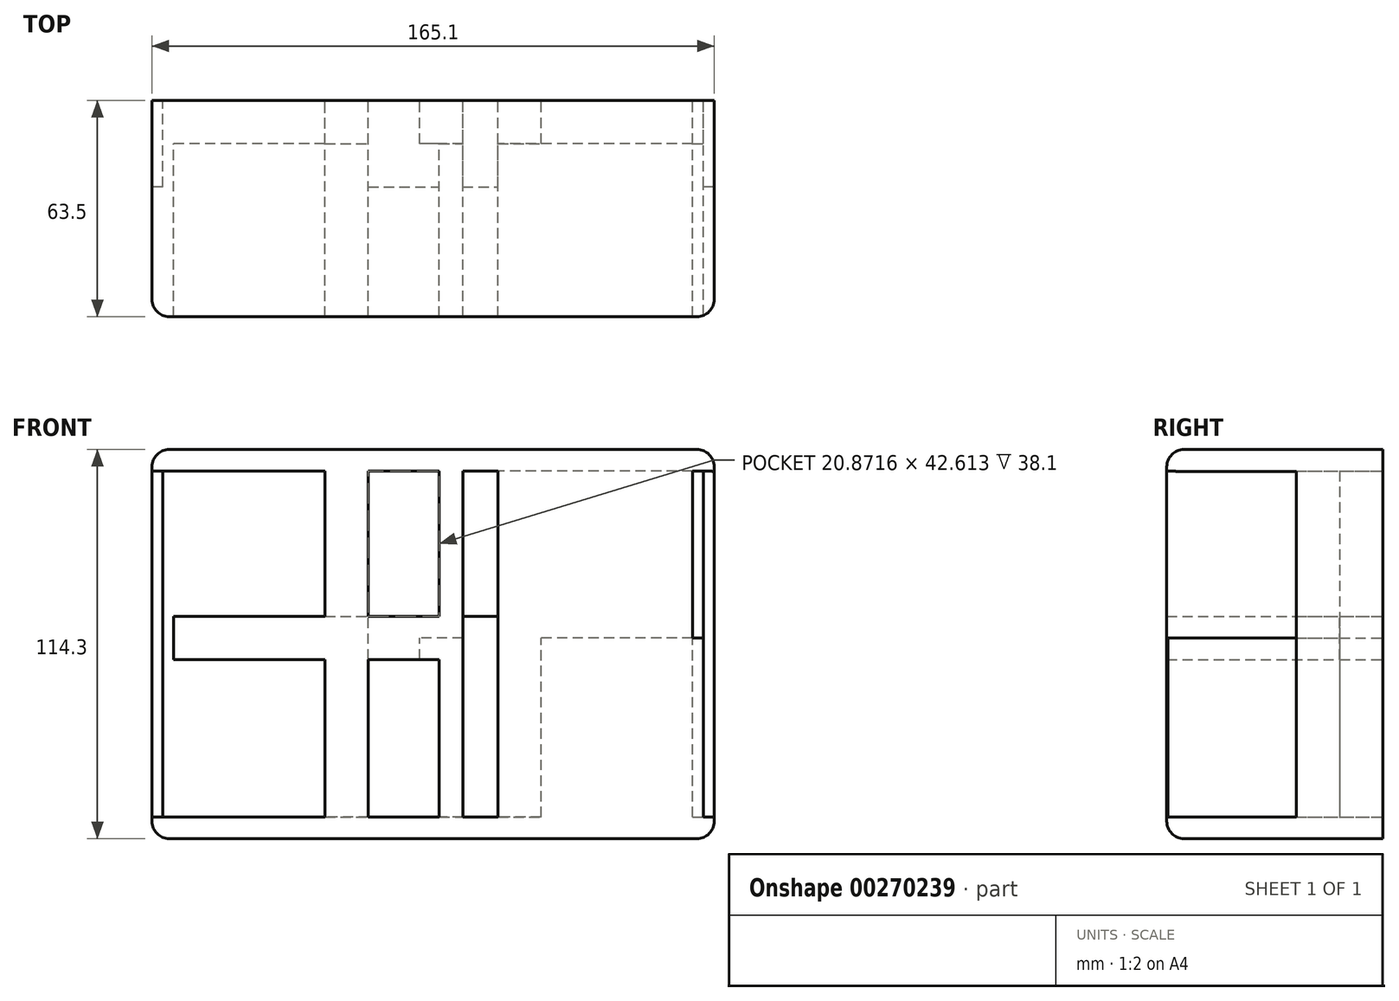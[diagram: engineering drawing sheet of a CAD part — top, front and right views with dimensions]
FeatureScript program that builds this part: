
annotation { "Feature Type Name" : "Feature", "Feature Type Description" : "" }
export const myFeature = defineFeature(function(context is Context, id is Id, definition is map)
    precondition{}
    {
        {
            var Q0;
            Q0=qCreatedBy(makeId("Front.planeOp"),FACE);
            var sketch = newSketch(context, id + "F0", { "sketchPlane" : qUnion([Q0])});
            skLineSegment(sketch, "E0", {"start": v(0, 0) * mm, "end": v(0, 48.96) * mm});
            skLineSegment(sketch, "E1", {"start": v(0, 48.96) * mm, "end": v(0, -52.64) * mm});
            skLineSegment(sketch, "E2", {"start": v(0, 0) * mm, "end": v(-78.02, 0) * mm});
            skLineSegment(sketch, "E3", {"start": v(-78.02, 0) * mm, "end": v(74.38, 0) * mm});
            skLineSegment(sketch, "E4.bottom", {"start": v(-78.02, 0) * mm, "end": v(0, 0) * mm});
            skLineSegment(sketch, "E4.top", {"start": v(-78.02, 48.96) * mm, "end": v(0, 48.96) * mm});
            skLineSegment(sketch, "E4.left", {"start": v(-78.02, 0) * mm, "end": v(-78.02, 48.96) * mm});
            skLineSegment(sketch, "E5.bottom", {"start": v(0, 48.96) * mm, "end": v(74.38, 48.96) * mm});
            skLineSegment(sketch, "E5.top", {"start": v(0, 0) * mm, "end": v(74.38, 0) * mm});
            skLineSegment(sketch, "E5.right", {"start": v(74.38, 48.96) * mm, "end": v(74.38, 0) * mm});
            skLineSegment(sketch, "E6.bottom", {"start": v(74.38, 0) * mm, "end": v(0, 0) * mm});
            skLineSegment(sketch, "E6.top", {"start": v(74.38, -52.64) * mm, "end": v(0, -52.64) * mm});
            skLineSegment(sketch, "E6.left", {"start": v(74.38, 0) * mm, "end": v(74.38, -52.64) * mm});
            skLineSegment(sketch, "E6.right", {"start": v(0, 0) * mm, "end": v(0, -52.64) * mm});
            skLineSegment(sketch, "E7.bottom", {"start": v(0, -52.64) * mm, "end": v(-78.02, -52.64) * mm});
            skLineSegment(sketch, "E7.right", {"start": v(-78.02, -52.64) * mm, "end": v(-78.02, 0) * mm});
            skLineSegment(sketch, "E8", {"start": v(0, 48.96) * mm, "end": v(0, 55.31) * mm});
            skLineSegment(sketch, "E9", {"start": v(-78.02, 0) * mm, "end": v(-84.37, 0) * mm});
            skLineSegment(sketch, "E10", {"start": v(0, -52.64) * mm, "end": v(0, -58.99) * mm});
            skLineSegment(sketch, "E11", {"start": v(74.38, 0) * mm, "end": v(80.73, 0) * mm});
            skLineSegment(sketch, "E12.top", {"start": v(-78.02, 55.31) * mm, "end": v(0, 55.31) * mm});
            skLineSegment(sketch, "E12.left", {"start": v(-78.02, 48.96) * mm, "end": v(-78.02, 55.31) * mm});
            skLineSegment(sketch, "E13.bottom", {"start": v(74.38, 48.96) * mm, "end": v(0, 48.96) * mm});
            skLineSegment(sketch, "E13.top", {"start": v(74.38, 55.31) * mm, "end": v(0, 55.31) * mm});
            skLineSegment(sketch, "E13.left", {"start": v(74.38, 48.96) * mm, "end": v(74.38, 55.31) * mm});
            skLineSegment(sketch, "E14.bottom", {"start": v(80.73, 0) * mm, "end": v(74.38, 0) * mm});
            skLineSegment(sketch, "E14.top", {"start": v(80.73, 55.31) * mm, "end": v(74.38, 55.31) * mm});
            skLineSegment(sketch, "E14.left", {"start": v(80.73, 0) * mm, "end": v(80.73, 55.31) * mm});
            skLineSegment(sketch, "E14.right", {"start": v(74.38, 0) * mm, "end": v(74.38, 55.31) * mm});
            skLineSegment(sketch, "E15.top", {"start": v(80.73, -52.64) * mm, "end": v(74.38, -52.64) * mm});
            skLineSegment(sketch, "E15.left", {"start": v(80.73, 0) * mm, "end": v(80.73, -52.64) * mm});
            skLineSegment(sketch, "E16.bottom", {"start": v(0, -58.99) * mm, "end": v(80.73, -58.99) * mm});
            skLineSegment(sketch, "E16.top", {"start": v(0, -52.64) * mm, "end": v(80.73, -52.64) * mm});
            skLineSegment(sketch, "E16.left", {"start": v(0, -58.99) * mm, "end": v(0, -52.64) * mm});
            skLineSegment(sketch, "E16.right", {"start": v(80.73, -58.99) * mm, "end": v(80.73, -52.64) * mm});
            skLineSegment(sketch, "E17.bottom", {"start": v(-78.02, -52.64) * mm, "end": v(0, -52.64) * mm});
            skLineSegment(sketch, "E17.top", {"start": v(-78.02, -58.99) * mm, "end": v(0, -58.99) * mm});
            skLineSegment(sketch, "E17.left", {"start": v(-78.02, -52.64) * mm, "end": v(-78.02, -58.99) * mm});
            skLineSegment(sketch, "E18.bottom", {"start": v(-84.37, 0) * mm, "end": v(-78.02, 0) * mm});
            skLineSegment(sketch, "E18.top", {"start": v(-84.37, -58.99) * mm, "end": v(-78.02, -58.99) * mm});
            skLineSegment(sketch, "E18.left", {"start": v(-84.37, 0) * mm, "end": v(-84.37, -58.99) * mm});
            skLineSegment(sketch, "E18.right", {"start": v(-78.02, 0) * mm, "end": v(-78.02, -58.99) * mm});
            skLineSegment(sketch, "E19.bottom", {"start": v(-78.02, 55.31) * mm, "end": v(-84.37, 55.31) * mm});
            skLineSegment(sketch, "E19.left", {"start": v(-78.02, 55.31) * mm, "end": v(-78.02, 0) * mm});
            skLineSegment(sketch, "E19.right", {"start": v(-84.37, 55.31) * mm, "end": v(-84.37, 0) * mm});
            skLineSegment(sketch, "E20", {"start": v(-78.02, -52.64) * mm, "end": v(-27.22, -52.64) * mm});
            skLineSegment(sketch, "E21", {"start": v(-27.22, -52.64) * mm, "end": v(74.38, -52.64) * mm});
            skLineSegment(sketch, "E22", {"start": v(74.38, -52.64) * mm, "end": v(23.58, -52.64) * mm});
            skLineSegment(sketch, "E23", {"start": v(-27.22, -52.64) * mm, "end": v(-27.22, 48.96) * mm});
            skLineSegment(sketch, "E24", {"start": v(23.58, -52.64) * mm, "end": v(23.58, 48.96) * mm});
            skLineSegment(sketch, "E25", {"start": v(0, 48.96) * mm, "end": v(-5.81, 48.96) * mm});
            skLineSegment(sketch, "E26", {"start": v(-5.81, 48.96) * mm, "end": v(6.89, 48.96) * mm});
            skLineSegment(sketch, "E27", {"start": v(-5.81, 48.96) * mm, "end": v(-5.81, -52.64) * mm});
            skLineSegment(sketch, "E28", {"start": v(6.89, 48.96) * mm, "end": v(6.89, -52.64) * mm});
            skLineSegment(sketch, "E29", {"start": v(-27.22, 48.96) * mm, "end": v(-33.57, 48.96) * mm});
            skLineSegment(sketch, "E30", {"start": v(-33.57, 48.96) * mm, "end": v(-20.87, 48.96) * mm});
            skLineSegment(sketch, "E31", {"start": v(23.58, 48.96) * mm, "end": v(17.23, 48.96) * mm});
            skLineSegment(sketch, "E32", {"start": v(17.23, 48.96) * mm, "end": v(29.93, 48.96) * mm});
            skLineSegment(sketch, "E33", {"start": v(-33.57, 48.96) * mm, "end": v(-33.57, -52.64) * mm});
            skLineSegment(sketch, "E34", {"start": v(-20.87, 48.96) * mm, "end": v(-20.87, -52.64) * mm});
            skLineSegment(sketch, "E35", {"start": v(17.23, 48.96) * mm, "end": v(17.23, -52.64) * mm});
            skLineSegment(sketch, "E36", {"start": v(29.93, 48.96) * mm, "end": v(29.93, -52.64) * mm});
            skLineSegment(sketch, "E37", {"start": v(74.38, 0) * mm, "end": v(74.38, 6.35) * mm});
            skLineSegment(sketch, "E38", {"start": v(74.38, 6.35) * mm, "end": v(74.38, -6.35) * mm});
            skLineSegment(sketch, "E39", {"start": v(74.38, -6.35) * mm, "end": v(-78.02, -6.35) * mm});
            skLineSegment(sketch, "E40", {"start": v(74.38, 6.35) * mm, "end": v(-78.02, 6.35) * mm});
            skLineSegment(sketch, "E41", {"start": v(77.55, -52.64) * mm, "end": v(77.55, 55.31) * mm});
            skLineSegment(sketch, "E42", {"start": v(80.73, 48.9) * mm, "end": v(74.38, 48.96) * mm});
            skLineSegment(sketch, "E43", {"start": v(-81.2, 55.31) * mm, "end": v(-81.2, -58.99) * mm});
            skLineSegment(sketch, "E44", {"start": v(-78.02, -52.64) * mm, "end": v(-84.37, -52.64) * mm});
            skLineSegment(sketch, "E45", {"start": v(-78.02, 48.96) * mm, "end": v(-84.37, 48.96) * mm});
            skSolve(sketch);
        }
        {
            var Q0;
            {var subQ2=sQuery(id+"F0.wireOp",EDGE,"E17.top");Q0=makeQuery(id+"F0.imprint","IMPRINT",FACE,{"disambiguationData":[TD([[makeQuery(id+"F0.imprint","IMPRINT",EDGE,{"derivedFrom":subQ2}),1.0]])]});}
            var Q1;
            {var subQ3=sQuery(id+"F0.wireOp",EDGE,"E19.bottom");Q1=makeQuery(id+"F0.imprint","IMPRINT",FACE,{"disambiguationData":[TD([[makeQuery(id+"F0.imprint","IMPRINT",EDGE,{"derivedFrom":subQ3}),1.0]])]});}
            var Q2;
            {var subQ1=sQuery(id+"F0.wireOp",EDGE,"E12.top");Q2=makeQuery(id+"F0.imprint","IMPRINT",FACE,{"disambiguationData":[TD([[makeQuery(id+"F0.imprint","IMPRINT",EDGE,{"derivedFrom":subQ1}),-1.0]])]});}
            var Q3;
            {var subQ4=sQuery(id+"F0.wireOp",EDGE,"E13.top");Q3=makeQuery(id+"F0.imprint","IMPRINT",FACE,{"disambiguationData":[TD([[makeQuery(id+"F0.imprint","IMPRINT",EDGE,{"derivedFrom":subQ4}),1.0]])]});}
            var Q4;
            {var subQ2=sQuery(id+"F0.wireOp",EDGE,"E14.top");Q4=makeQuery(id+"F0.imprint","IMPRINT",FACE,{"disambiguationData":[TD([[makeQuery(id+"F0.imprint","IMPRINT",EDGE,{"derivedFrom":subQ2}),1.0]])]});}
            var Q5;
            Q5=makeQuery(id+"F0.imprint","IMPRINT",FACE,{"disambiguationData":[TD([[makeQuery(id+"F0.imprint","IMPRINT",EDGE,{"derivedFrom":sQuery(id+"F0.wireOp",EDGE,"E16.bottom")}),1.0]])]});
            var Q6;
            {var subQ1=sQuery(id+"F0.wireOp",EDGE,"E18.top");Q6=makeQuery(id+"F0.imprint","IMPRINT",FACE,{"disambiguationData":[TD([[makeQuery(id+"F0.imprint","IMPRINT",EDGE,{"derivedFrom":subQ1}),1.0]])]});}
            var Q7;
            {var subQ0=sQuery(id+"F0.wireOp",EDGE,"E23");var subQ1=sQuery(id+"F0.wireOp",EDGE,"E2");var subQ2=makeQuery(id+"F0.imprint","INTERSECT",VERTEX,{"derivedFrom":[subQ1,subQ0]});Q7=makeQuery(id+"F0.imprint","IMPRINT",FACE,{"disambiguationData":[TD([[makeQuery(id+"F0.imprint","IMPRINT",EDGE,{"disambiguationData":[TD([[subQ2,-1.0]])],"derivedFrom":subQ1}),-1.0]])]});}
            var Q8;
            {var subQ0=sQuery(id+"F0.wireOp",EDGE,"E34");var subQ1=sQuery(id+"F0.wireOp",EDGE,"E2");var subQ2=makeQuery(id+"F0.imprint","INTERSECT",VERTEX,{"derivedFrom":[subQ1,subQ0]});Q8=makeQuery(id+"F0.imprint","IMPRINT",FACE,{"disambiguationData":[TD([[makeQuery(id+"F0.imprint","IMPRINT",EDGE,{"disambiguationData":[TD([[subQ2,-1.0]])],"derivedFrom":subQ1}),-1.0]])]});}
            var Q9;
            {var subQ0=sQuery(id+"F0.wireOp",EDGE,"E23");var subQ1=sQuery(id+"F0.wireOp",EDGE,"E2");var subQ2=makeQuery(id+"F0.imprint","INTERSECT",VERTEX,{"derivedFrom":[subQ1,subQ0]});Q9=makeQuery(id+"F0.imprint","IMPRINT",FACE,{"disambiguationData":[TD([[makeQuery(id+"F0.imprint","IMPRINT",EDGE,{"disambiguationData":[TD([[subQ2,-1.0]])],"derivedFrom":subQ1}),1.0]])]});}
            var Q10;
            {var subQ0=sQuery(id+"F0.wireOp",EDGE,"E34");var subQ1=sQuery(id+"F0.wireOp",EDGE,"E2");var subQ2=makeQuery(id+"F0.imprint","INTERSECT",VERTEX,{"derivedFrom":[subQ1,subQ0]});Q10=makeQuery(id+"F0.imprint","IMPRINT",FACE,{"disambiguationData":[TD([[makeQuery(id+"F0.imprint","IMPRINT",EDGE,{"disambiguationData":[TD([[subQ2,-1.0]])],"derivedFrom":subQ1}),1.0]])]});}
            var Q11;
            {var subQ0=sQuery(id+"F0.wireOp",EDGE,"E24");var subQ1=sQuery(id+"F0.wireOp",EDGE,"E6.bottom");var subQ2=makeQuery(id+"F0.imprint","INTERSECT",VERTEX,{"derivedFrom":[subQ1,subQ0]});Q11=makeQuery(id+"F0.imprint","IMPRINT",FACE,{"disambiguationData":[TD([[makeQuery(id+"F0.imprint","IMPRINT",EDGE,{"disambiguationData":[TD([[subQ2,-1.0]])],"derivedFrom":subQ1}),-1.0]])]});}
            var Q12;
            {var subQ0=sQuery(id+"F0.wireOp",EDGE,"E24");var subQ1=sQuery(id+"F0.wireOp",EDGE,"E6.bottom");var subQ2=makeQuery(id+"F0.imprint","INTERSECT",VERTEX,{"derivedFrom":[subQ1,subQ0]});Q12=makeQuery(id+"F0.imprint","IMPRINT",FACE,{"disambiguationData":[TD([[makeQuery(id+"F0.imprint","IMPRINT",EDGE,{"disambiguationData":[TD([[subQ2,-1.0]])],"derivedFrom":subQ1}),1.0]])]});}
            var Q13;
            {var subQ0=sQuery(id+"F0.wireOp",EDGE,"E36");var subQ1=sQuery(id+"F0.wireOp",EDGE,"E6.bottom");var subQ2=makeQuery(id+"F0.imprint","INTERSECT",VERTEX,{"derivedFrom":[subQ1,subQ0]});Q13=makeQuery(id+"F0.imprint","IMPRINT",FACE,{"disambiguationData":[TD([[makeQuery(id+"F0.imprint","IMPRINT",EDGE,{"disambiguationData":[TD([[subQ2,-1.0]])],"derivedFrom":subQ1}),1.0]])]});}
            var Q14;
            {var subQ0=sQuery(id+"F0.wireOp",EDGE,"E36");var subQ1=sQuery(id+"F0.wireOp",EDGE,"E6.bottom");var subQ2=makeQuery(id+"F0.imprint","INTERSECT",VERTEX,{"derivedFrom":[subQ1,subQ0]});Q14=makeQuery(id+"F0.imprint","IMPRINT",FACE,{"disambiguationData":[TD([[makeQuery(id+"F0.imprint","IMPRINT",EDGE,{"disambiguationData":[TD([[subQ2,-1.0]])],"derivedFrom":subQ1}),-1.0]])]});}
            var Q15;
            {var subQ1=sQuery(id+"F0.wireOp",EDGE,"E2");var subQ3=sQuery(id+"F0.wireOp",EDGE,"E33");var subQ4=makeQuery(id+"F0.imprint","INTERSECT",VERTEX,{"derivedFrom":[subQ1,subQ3]});Q15=makeQuery(id+"F0.imprint","IMPRINT",FACE,{"disambiguationData":[TD([[makeQuery(id+"F0.imprint","IMPRINT",EDGE,{"disambiguationData":[TD([[subQ4,1.0]])],"derivedFrom":subQ3}),-1.0]])]});}
            var Q16;
            {var subQ1=sQuery(id+"F0.wireOp",EDGE,"E2");var subQ3=sQuery(id+"F0.wireOp",EDGE,"E33");var subQ4=makeQuery(id+"F0.imprint","INTERSECT",VERTEX,{"derivedFrom":[subQ1,subQ3]});Q16=makeQuery(id+"F0.imprint","IMPRINT",FACE,{"disambiguationData":[TD([[makeQuery(id+"F0.imprint","IMPRINT",EDGE,{"disambiguationData":[TD([[subQ4,-1.0]])],"derivedFrom":subQ3}),-1.0]])]});}
            var Q17;
            {var subQ0=sQuery(id+"F0.wireOp",EDGE,"E27");var subQ1=sQuery(id+"F0.wireOp",EDGE,"E2");var subQ2=makeQuery(id+"F0.imprint","INTERSECT",VERTEX,{"derivedFrom":[subQ1,subQ0]});Q17=makeQuery(id+"F0.imprint","IMPRINT",FACE,{"disambiguationData":[TD([[makeQuery(id+"F0.imprint","IMPRINT",EDGE,{"disambiguationData":[TD([[subQ2,-1.0]])],"derivedFrom":subQ1}),-1.0]])]});}
            var Q18;
            {var subQ0=sQuery(id+"F0.wireOp",EDGE,"E27");var subQ1=sQuery(id+"F0.wireOp",EDGE,"E2");var subQ2=makeQuery(id+"F0.imprint","INTERSECT",VERTEX,{"derivedFrom":[subQ1,subQ0]});Q18=makeQuery(id+"F0.imprint","IMPRINT",FACE,{"disambiguationData":[TD([[makeQuery(id+"F0.imprint","IMPRINT",EDGE,{"disambiguationData":[TD([[subQ2,-1.0]])],"derivedFrom":subQ1}),1.0]])]});}
            var Q19;
            {var subQ0=sQuery(id+"F0.wireOp",EDGE,"E2");var subQ5=sQuery(id+"F0.wireOp",EDGE,"E27");var subQ6=makeQuery(id+"F0.imprint","INTERSECT",VERTEX,{"derivedFrom":[subQ0,subQ5]});Q19=makeQuery(id+"F0.imprint","IMPRINT",FACE,{"disambiguationData":[TD([[makeQuery(id+"F0.imprint","IMPRINT",EDGE,{"disambiguationData":[TD([[subQ6,1.0]])],"derivedFrom":subQ5}),1.0]])]});}
            var Q20;
            {var subQ0=sQuery(id+"F0.wireOp",EDGE,"E2");var subQ5=sQuery(id+"F0.wireOp",EDGE,"E27");var subQ6=makeQuery(id+"F0.imprint","INTERSECT",VERTEX,{"derivedFrom":[subQ0,subQ5]});Q20=makeQuery(id+"F0.imprint","IMPRINT",FACE,{"disambiguationData":[TD([[makeQuery(id+"F0.imprint","IMPRINT",EDGE,{"disambiguationData":[TD([[subQ6,-1.0]])],"derivedFrom":subQ5}),1.0]])]});}
            var Q21;
            {var subQ1=sQuery(id+"F0.wireOp",EDGE,"E6.bottom");var subQ3=sQuery(id+"F0.wireOp",EDGE,"E28");var subQ4=makeQuery(id+"F0.imprint","INTERSECT",VERTEX,{"derivedFrom":[subQ1,subQ3]});Q21=makeQuery(id+"F0.imprint","IMPRINT",FACE,{"disambiguationData":[TD([[makeQuery(id+"F0.imprint","IMPRINT",EDGE,{"disambiguationData":[TD([[subQ4,-1.0]])],"derivedFrom":subQ3}),-1.0]])]});}
            var Q22;
            {var subQ0=sQuery(id+"F0.wireOp",EDGE,"E6.bottom");var subQ5=sQuery(id+"F0.wireOp",EDGE,"E28");var subQ6=makeQuery(id+"F0.imprint","INTERSECT",VERTEX,{"derivedFrom":[subQ0,subQ5]});Q22=makeQuery(id+"F0.imprint","IMPRINT",FACE,{"disambiguationData":[TD([[makeQuery(id+"F0.imprint","IMPRINT",EDGE,{"disambiguationData":[TD([[subQ6,1.0]])],"derivedFrom":subQ5}),-1.0]])]});}
            var Q23;
            {var subQ0=sQuery(id+"F0.wireOp",EDGE,"E35");var subQ1=sQuery(id+"F0.wireOp",EDGE,"E6.bottom");var subQ2=makeQuery(id+"F0.imprint","INTERSECT",VERTEX,{"derivedFrom":[subQ1,subQ0]});Q23=makeQuery(id+"F0.imprint","IMPRINT",FACE,{"disambiguationData":[TD([[makeQuery(id+"F0.imprint","IMPRINT",EDGE,{"disambiguationData":[TD([[subQ2,-1.0]])],"derivedFrom":subQ1}),-1.0]])]});}
            var Q24;
            {var subQ0=sQuery(id+"F0.wireOp",EDGE,"E35");var subQ1=sQuery(id+"F0.wireOp",EDGE,"E6.bottom");var subQ2=makeQuery(id+"F0.imprint","INTERSECT",VERTEX,{"derivedFrom":[subQ1,subQ0]});Q24=makeQuery(id+"F0.imprint","IMPRINT",FACE,{"disambiguationData":[TD([[makeQuery(id+"F0.imprint","IMPRINT",EDGE,{"disambiguationData":[TD([[subQ2,-1.0]])],"derivedFrom":subQ1}),1.0]])]});}
            var Q25;
            {var subQ1=sQuery(id+"F0.wireOp",EDGE,"E6.bottom");var subQ3=sQuery(id+"F0.wireOp",EDGE,"E36");var subQ4=makeQuery(id+"F0.imprint","INTERSECT",VERTEX,{"derivedFrom":[subQ1,subQ3]});Q25=makeQuery(id+"F0.imprint","IMPRINT",FACE,{"disambiguationData":[TD([[makeQuery(id+"F0.imprint","IMPRINT",EDGE,{"disambiguationData":[TD([[subQ4,1.0]])],"derivedFrom":subQ3}),1.0]])]});}
            var Q26;
            {var subQ1=sQuery(id+"F0.wireOp",EDGE,"E6.bottom");var subQ3=sQuery(id+"F0.wireOp",EDGE,"E36");var subQ4=makeQuery(id+"F0.imprint","INTERSECT",VERTEX,{"derivedFrom":[subQ1,subQ3]});Q26=makeQuery(id+"F0.imprint","IMPRINT",FACE,{"disambiguationData":[TD([[makeQuery(id+"F0.imprint","IMPRINT",EDGE,{"disambiguationData":[TD([[subQ4,-1.0]])],"derivedFrom":subQ3}),1.0]])]});}
            var Q27;
            {var subQ0=sQuery(id+"F0.wireOp",EDGE,"E30");var subQ1=sQuery(id+"F0.wireOp",EDGE,"E23");var subQ2=makeQuery(id+"F0.imprint","INTERSECT",VERTEX,{"derivedFrom":[subQ1,subQ0]});Q27=makeQuery(id+"F0.imprint","IMPRINT",FACE,{"disambiguationData":[TD([[makeQuery(id+"F0.imprint","IMPRINT",EDGE,{"disambiguationData":[TD([[subQ2,1.0]])],"derivedFrom":subQ1}),1.0]])]});}
            var Q28;
            {var subQ0=sQuery(id+"F0.wireOp",EDGE,"E30");var subQ1=sQuery(id+"F0.wireOp",EDGE,"E23");var subQ2=makeQuery(id+"F0.imprint","INTERSECT",VERTEX,{"derivedFrom":[subQ1,subQ0]});Q28=makeQuery(id+"F0.imprint","IMPRINT",FACE,{"disambiguationData":[TD([[makeQuery(id+"F0.imprint","IMPRINT",EDGE,{"disambiguationData":[TD([[subQ2,1.0]])],"derivedFrom":subQ1}),-1.0]])]});}
            var Q29;
            {var subQ1=sQuery(id+"F0.wireOp",EDGE,"E20");var subQ3=sQuery(id+"F0.wireOp",EDGE,"E33");var subQ4=makeQuery(id+"F0.imprint","INTERSECT",VERTEX,{"derivedFrom":[subQ1,subQ3]});Q29=makeQuery(id+"F0.imprint","IMPRINT",FACE,{"disambiguationData":[TD([[makeQuery(id+"F0.imprint","IMPRINT",EDGE,{"disambiguationData":[TD([[subQ4,1.0]])],"derivedFrom":subQ3}),1.0]])]});}
            var Q30;
            {var subQ1=sQuery(id+"F0.wireOp",EDGE,"E21");var subQ3=sQuery(id+"F0.wireOp",EDGE,"E34");var subQ4=makeQuery(id+"F0.imprint","INTERSECT",VERTEX,{"derivedFrom":[subQ1,subQ3]});Q30=makeQuery(id+"F0.imprint","IMPRINT",FACE,{"disambiguationData":[TD([[makeQuery(id+"F0.imprint","IMPRINT",EDGE,{"disambiguationData":[TD([[subQ4,1.0]])],"derivedFrom":subQ3}),-1.0]])]});}
            var Q31;
            {var subQ0=sQuery(id+"F0.wireOp",EDGE,"E32");var subQ1=sQuery(id+"F0.wireOp",EDGE,"E24");var subQ2=makeQuery(id+"F0.imprint","INTERSECT",VERTEX,{"derivedFrom":[subQ1,subQ0]});Q31=makeQuery(id+"F0.imprint","IMPRINT",FACE,{"disambiguationData":[TD([[makeQuery(id+"F0.imprint","IMPRINT",EDGE,{"disambiguationData":[TD([[subQ2,1.0]])],"derivedFrom":subQ1}),1.0]])]});}
            var Q32;
            {var subQ0=sQuery(id+"F0.wireOp",EDGE,"E32");var subQ1=sQuery(id+"F0.wireOp",EDGE,"E24");var subQ2=makeQuery(id+"F0.imprint","INTERSECT",VERTEX,{"derivedFrom":[subQ1,subQ0]});Q32=makeQuery(id+"F0.imprint","IMPRINT",FACE,{"disambiguationData":[TD([[makeQuery(id+"F0.imprint","IMPRINT",EDGE,{"disambiguationData":[TD([[subQ2,1.0]])],"derivedFrom":subQ1}),-1.0]])]});}
            var Q33;
            {var subQ1=sQuery(id+"F0.wireOp",EDGE,"E21");var subQ3=sQuery(id+"F0.wireOp",EDGE,"E35");var subQ4=makeQuery(id+"F0.imprint","INTERSECT",VERTEX,{"derivedFrom":[subQ1,subQ3]});Q33=makeQuery(id+"F0.imprint","IMPRINT",FACE,{"disambiguationData":[TD([[makeQuery(id+"F0.imprint","IMPRINT",EDGE,{"disambiguationData":[TD([[subQ4,1.0]])],"derivedFrom":subQ3}),1.0]])]});}
            var Q34;
            {var subQ1=sQuery(id+"F0.wireOp",EDGE,"E22");var subQ3=sQuery(id+"F0.wireOp",EDGE,"E36");var subQ4=makeQuery(id+"F0.imprint","INTERSECT",VERTEX,{"derivedFrom":[subQ1,subQ3]});Q34=makeQuery(id+"F0.imprint","IMPRINT",FACE,{"disambiguationData":[TD([[makeQuery(id+"F0.imprint","IMPRINT",EDGE,{"disambiguationData":[TD([[subQ4,1.0]])],"derivedFrom":subQ3}),-1.0]])]});}
            var Q35;
            {var subQ0=sQuery(id+"F0.wireOp",EDGE,"E41");var subQ1=sQuery(id+"F0.wireOp",EDGE,"E14.bottom");var subQ2=makeQuery(id+"F0.imprint","INTERSECT",VERTEX,{"derivedFrom":[subQ1,subQ0]});Q35=makeQuery(id+"F0.imprint","IMPRINT",FACE,{"disambiguationData":[TD([[makeQuery(id+"F0.imprint","IMPRINT",EDGE,{"disambiguationData":[TD([[subQ2,-1.0]])],"derivedFrom":subQ0}),1.0]])]});}
            var Q36;
            {var subQ3=sQuery(id+"F0.wireOp",EDGE,"E6.left");Q36=makeQuery(id+"F0.imprint","IMPRINT",FACE,{"disambiguationData":[TD([[makeQuery(id+"F0.imprint","IMPRINT",EDGE,{"derivedFrom":subQ3}),1.0]])]});}
            var Q37;
            {var subQ0=sQuery(id+"F0.wireOp",EDGE,"E43");var subQ1=sQuery(id+"F0.wireOp",EDGE,"E9");var subQ2=makeQuery(id+"F0.imprint","INTERSECT",VERTEX,{"derivedFrom":[subQ1,subQ0]});Q37=makeQuery(id+"F0.imprint","IMPRINT",FACE,{"disambiguationData":[TD([[makeQuery(id+"F0.imprint","IMPRINT",EDGE,{"disambiguationData":[TD([[subQ2,1.0]])],"derivedFrom":subQ0}),1.0]])]});}
            var Q38;
            {var subQ0=sQuery(id+"F0.wireOp",EDGE,"E43");var subQ1=sQuery(id+"F0.wireOp",EDGE,"E9");var subQ2=makeQuery(id+"F0.imprint","INTERSECT",VERTEX,{"derivedFrom":[subQ1,subQ0]});Q38=makeQuery(id+"F0.imprint","IMPRINT",FACE,{"disambiguationData":[TD([[makeQuery(id+"F0.imprint","IMPRINT",EDGE,{"disambiguationData":[TD([[subQ2,-1.0]])],"derivedFrom":subQ0}),1.0]])]});}
            extrude(context, id + "F1", {"entities" : qUnion([Q0, Q1, Q2, Q3, Q4, Q5, Q6, Q7, Q8, Q9, Q10, Q11, Q12, Q13, Q14, Q15, Q16, Q17, Q18, Q19, Q20, Q21, Q22, Q23, Q24, Q25, Q26, Q27, Q28, Q29, Q30, Q31, Q32, Q33, Q34, Q35, Q36, Q37, Q38]), "depth" : 50.8 * mm});
        }
        {
            var Q0;
            Q0 = qSketchRegion(id + "F0", true);
            var Q1;
            {var subQ0=sQuery(id+"F0.wireOp",EDGE,"E19.left");var subQ5=sQuery(id+"F0.wireOp",EDGE,"E4.top");var subQ6=makeQuery(id+"F0.imprint","INTERSECT",VERTEX,{"derivedFrom":[subQ5,subQ0]});Q1=makeQuery(id+"F0.imprint","IMPRINT",FACE,{"disambiguationData":[TD([[makeQuery(id+"F0.imprint","IMPRINT",EDGE,{"disambiguationData":[TD([[subQ6,-1.0]])],"derivedFrom":subQ5}),-1.0]])]});}
            var Q2;
            {var subQ0=sQuery(id+"F0.wireOp",EDGE,"E18.right");var subQ5=sQuery(id+"F0.wireOp",EDGE,"E20");var subQ6=makeQuery(id+"F0.imprint","INTERSECT",VERTEX,{"derivedFrom":[subQ0,subQ5]});Q2=makeQuery(id+"F0.imprint","IMPRINT",FACE,{"disambiguationData":[TD([[makeQuery(id+"F0.imprint","IMPRINT",EDGE,{"disambiguationData":[TD([[subQ6,-1.0]])],"derivedFrom":subQ5}),1.0]])]});}
            var Q3;
            {var subQ0=sQuery(id+"F0.wireOp",EDGE,"E27");var subQ1=sQuery(id+"F0.wireOp",EDGE,"E2");var subQ2=makeQuery(id+"F0.imprint","INTERSECT",VERTEX,{"derivedFrom":[subQ1,subQ0]});Q3=makeQuery(id+"F0.imprint","IMPRINT",FACE,{"disambiguationData":[TD([[makeQuery(id+"F0.imprint","IMPRINT",EDGE,{"disambiguationData":[TD([[subQ2,-1.0]])],"derivedFrom":subQ1}),1.0]])]});}
            var Q4;
            {var subQ0=sQuery(id+"F0.wireOp",EDGE,"E6.right");Q4=makeQuery(id+"F0.imprint","IMPRINT",FACE,{"disambiguationData":[TD([[makeQuery(id+"F0.imprint","IMPRINT",EDGE,{"derivedFrom":subQ0}),-1.0]])]});}
            var Q5;
            {var subQ0=sQuery(id+"F0.wireOp",EDGE,"E6.right");Q5=makeQuery(id+"F0.imprint","IMPRINT",FACE,{"disambiguationData":[TD([[makeQuery(id+"F0.imprint","IMPRINT",EDGE,{"derivedFrom":subQ0}),1.0]])]});}
            var Q6;
            {var subQ0=sQuery(id+"F0.wireOp",EDGE,"E35");var subQ1=sQuery(id+"F0.wireOp",EDGE,"E6.bottom");var subQ2=makeQuery(id+"F0.imprint","INTERSECT",VERTEX,{"derivedFrom":[subQ1,subQ0]});Q6=makeQuery(id+"F0.imprint","IMPRINT",FACE,{"disambiguationData":[TD([[makeQuery(id+"F0.imprint","IMPRINT",EDGE,{"disambiguationData":[TD([[subQ2,-1.0]])],"derivedFrom":subQ1}),1.0]])]});}
            var Q7;
            {var subQ0=sQuery(id+"F0.wireOp",EDGE,"E35");var subQ1=sQuery(id+"F0.wireOp",EDGE,"E6.bottom");var subQ2=makeQuery(id+"F0.imprint","INTERSECT",VERTEX,{"derivedFrom":[subQ1,subQ0]});Q7=makeQuery(id+"F0.imprint","IMPRINT",FACE,{"disambiguationData":[TD([[makeQuery(id+"F0.imprint","IMPRINT",EDGE,{"disambiguationData":[TD([[subQ2,-1.0]])],"derivedFrom":subQ1}),-1.0]])]});}
            var Q8;
            {var subQ0=sQuery(id+"F0.wireOp",EDGE,"E0");Q8=makeQuery(id+"F0.imprint","IMPRINT",FACE,{"disambiguationData":[TD([[makeQuery(id+"F0.imprint","IMPRINT",EDGE,{"derivedFrom":subQ0}),-1.0]])]});}
            var Q9;
            {var subQ0=sQuery(id+"F0.wireOp",EDGE,"E0");Q9=makeQuery(id+"F0.imprint","IMPRINT",FACE,{"disambiguationData":[TD([[makeQuery(id+"F0.imprint","IMPRINT",EDGE,{"derivedFrom":subQ0}),1.0]])]});}
            var Q10;
            {var subQ0=sQuery(id+"F0.wireOp",EDGE,"E27");var subQ1=sQuery(id+"F0.wireOp",EDGE,"E2");var subQ2=makeQuery(id+"F0.imprint","INTERSECT",VERTEX,{"derivedFrom":[subQ1,subQ0]});Q10=makeQuery(id+"F0.imprint","IMPRINT",FACE,{"disambiguationData":[TD([[makeQuery(id+"F0.imprint","IMPRINT",EDGE,{"disambiguationData":[TD([[subQ2,-1.0]])],"derivedFrom":subQ1}),-1.0]])]});}
            var Q11;
            {var subQ0=sQuery(id+"F0.wireOp",EDGE,"E14.right");var subQ5=sQuery(id+"F0.wireOp",EDGE,"E13.bottom");var subQ7=makeQuery(id+"F0.imprint","INTERSECT",VERTEX,{"derivedFrom":[subQ5,subQ0]});Q11=makeQuery(id+"F0.imprint","IMPRINT",FACE,{"disambiguationData":[TD([[makeQuery(id+"F0.imprint","IMPRINT",EDGE,{"disambiguationData":[TD([[subQ7,-1.0]])],"derivedFrom":subQ5}),1.0]])]});}
            var Q12;
            {var subQ0=sQuery(id+"F0.wireOp",EDGE,"E6.left");Q12=makeQuery(id+"F0.imprint","IMPRINT",FACE,{"disambiguationData":[TD([[makeQuery(id+"F0.imprint","IMPRINT",EDGE,{"derivedFrom":subQ0}),-1.0]])]});}
            var Q13;
            {var subQ0=sQuery(id+"F0.wireOp",EDGE,"E27");var subQ5=sQuery(id+"F0.wireOp",EDGE,"E40");var subQ6=makeQuery(id+"F0.imprint","INTERSECT",VERTEX,{"derivedFrom":[subQ0,subQ5]});Q13=makeQuery(id+"F0.imprint","IMPRINT",FACE,{"disambiguationData":[TD([[makeQuery(id+"F0.imprint","IMPRINT",EDGE,{"disambiguationData":[TD([[subQ6,-1.0]])],"derivedFrom":subQ5}),-1.0]])]});}
            var Q14;
            {var subQ0=sQuery(id+"F0.wireOp",EDGE,"E28");var subQ5=sQuery(id+"F0.wireOp",EDGE,"E40");var subQ6=makeQuery(id+"F0.imprint","INTERSECT",VERTEX,{"derivedFrom":[subQ0,subQ5]});Q14=makeQuery(id+"F0.imprint","IMPRINT",FACE,{"disambiguationData":[TD([[makeQuery(id+"F0.imprint","IMPRINT",EDGE,{"disambiguationData":[TD([[subQ6,1.0]])],"derivedFrom":subQ5}),-1.0]])]});}
            var Q15;
            {var subQ0=sQuery(id+"F0.wireOp",EDGE,"E28");var subQ1=sQuery(id+"F0.wireOp",EDGE,"E21");var subQ2=makeQuery(id+"F0.imprint","INTERSECT",VERTEX,{"derivedFrom":[subQ1,subQ0]});Q15=makeQuery(id+"F0.imprint","IMPRINT",FACE,{"disambiguationData":[TD([[makeQuery(id+"F0.imprint","IMPRINT",EDGE,{"disambiguationData":[TD([[subQ2,-1.0]])],"derivedFrom":subQ1}),1.0]])]});}
            var Q16;
            {var subQ0=sQuery(id+"F0.wireOp",EDGE,"E27");var subQ1=sQuery(id+"F0.wireOp",EDGE,"E21");var subQ2=makeQuery(id+"F0.imprint","INTERSECT",VERTEX,{"derivedFrom":[subQ1,subQ0]});Q16=makeQuery(id+"F0.imprint","IMPRINT",FACE,{"disambiguationData":[TD([[makeQuery(id+"F0.imprint","IMPRINT",EDGE,{"disambiguationData":[TD([[subQ2,1.0]])],"derivedFrom":subQ1}),1.0]])]});}
            extrude(context, id + "F2", {"entities" : qUnion([Q0, Q1, Q2, Q3, Q4, Q5, Q6, Q7, Q8, Q9, Q10, Q11, Q12, Q13, Q14, Q15, Q16]), "operationType" : NewBodyOperationType.ADD, "endBound" : BoundingType.SYMMETRIC, "depth" : 25.4 * mm});
        }
        {
            var Q0;
            Q0=makeQuery(id+"F1.opExtrude","CAP_EDGE",EDGE,{"disambiguationData":[OSD([sQuery(id+"F0.wireOp",EDGE,"E14.left"),sQuery(id+"F0.wireOp",EDGE,"E15.left"),sQuery(id+"F0.wireOp",EDGE,"E16.right")])],"isStart":false});
            var Q1;
            Q1=makeQuery(id+"F1.opExtrude","CAP_EDGE",EDGE,{"disambiguationData":[OSD([sQuery(id+"F0.wireOp",EDGE,"E12.top"),sQuery(id+"F0.wireOp",EDGE,"E13.top"),sQuery(id+"F0.wireOp",EDGE,"E14.top"),sQuery(id+"F0.wireOp",EDGE,"E19.bottom")])],"isStart":false});
            var Q2;
            Q2=makeQuery(id+"F1.opExtrude","SWEPT_EDGE",EDGE,{"disambiguationData":[OSD([sQuery(id+"F0.wireOp",EDGE,"E14.top"),sQuery(id+"F0.wireOp",EDGE,"E14.left")])]});
            var Q3;
            Q3=makeQuery(id+"F1.opExtrude","CAP_EDGE",EDGE,{"disambiguationData":[OSD([sQuery(id+"F0.wireOp",EDGE,"E14.left"),sQuery(id+"F0.wireOp",EDGE,"E15.left"),sQuery(id+"F0.wireOp",EDGE,"E16.right")])],"isStart":true});
            var Q4;
            Q4=makeQuery(id+"F1.opExtrude","CAP_EDGE",EDGE,{"disambiguationData":[OSD([sQuery(id+"F0.wireOp",EDGE,"E12.top"),sQuery(id+"F0.wireOp",EDGE,"E13.top"),sQuery(id+"F0.wireOp",EDGE,"E14.top"),sQuery(id+"F0.wireOp",EDGE,"E19.bottom")])],"isStart":true});
            var Q5;
            Q5=makeQuery(id+"F1.opExtrude","SWEPT_EDGE",EDGE,{"disambiguationData":[OSD([sQuery(id+"F0.wireOp",EDGE,"E19.bottom"),sQuery(id+"F0.wireOp",EDGE,"E19.right")])]});
            var Q6;
            Q6=makeQuery(id+"F1.opExtrude","CAP_EDGE",EDGE,{"disambiguationData":[OSD([sQuery(id+"F0.wireOp",EDGE,"E16.bottom"),sQuery(id+"F0.wireOp",EDGE,"E17.top"),sQuery(id+"F0.wireOp",EDGE,"E18.top")])],"isStart":true});
            var Q7;
            Q7=makeQuery(id+"F1.opExtrude","CAP_EDGE",EDGE,{"disambiguationData":[OSD([sQuery(id+"F0.wireOp",EDGE,"E18.left"),sQuery(id+"F0.wireOp",EDGE,"E19.right")])],"isStart":true});
            var Q8;
            Q8=makeQuery(id+"F1.opExtrude","SWEPT_EDGE",EDGE,{"disambiguationData":[OSD([sQuery(id+"F0.wireOp",EDGE,"E16.bottom"),sQuery(id+"F0.wireOp",EDGE,"E16.right")])]});
            var Q9;
            Q9=makeQuery(id+"F1.opExtrude","CAP_EDGE",EDGE,{"disambiguationData":[OSD([sQuery(id+"F0.wireOp",EDGE,"E16.bottom"),sQuery(id+"F0.wireOp",EDGE,"E17.top"),sQuery(id+"F0.wireOp",EDGE,"E18.top")])],"isStart":false});
            var Q10;
            Q10=makeQuery(id+"F1.opExtrude","SWEPT_EDGE",EDGE,{"disambiguationData":[OSD([sQuery(id+"F0.wireOp",EDGE,"E18.top"),sQuery(id+"F0.wireOp",EDGE,"E18.left")])]});
            var Q11;
            Q11=makeQuery(id+"F1.opExtrude","CAP_EDGE",EDGE,{"disambiguationData":[OSD([sQuery(id+"F0.wireOp",EDGE,"E18.left"),sQuery(id+"F0.wireOp",EDGE,"E19.right")])],"isStart":false});
            fillet(context, id + "F3", {"entities" : qUnion([Q0, Q1, Q2, Q3, Q4, Q5, Q6, Q7, Q8, Q9, Q10, Q11]), "radius" : 5.08 * mm, "tangentPropagation" : true, "allowEdgeOverflow" : false});
        }
    });
